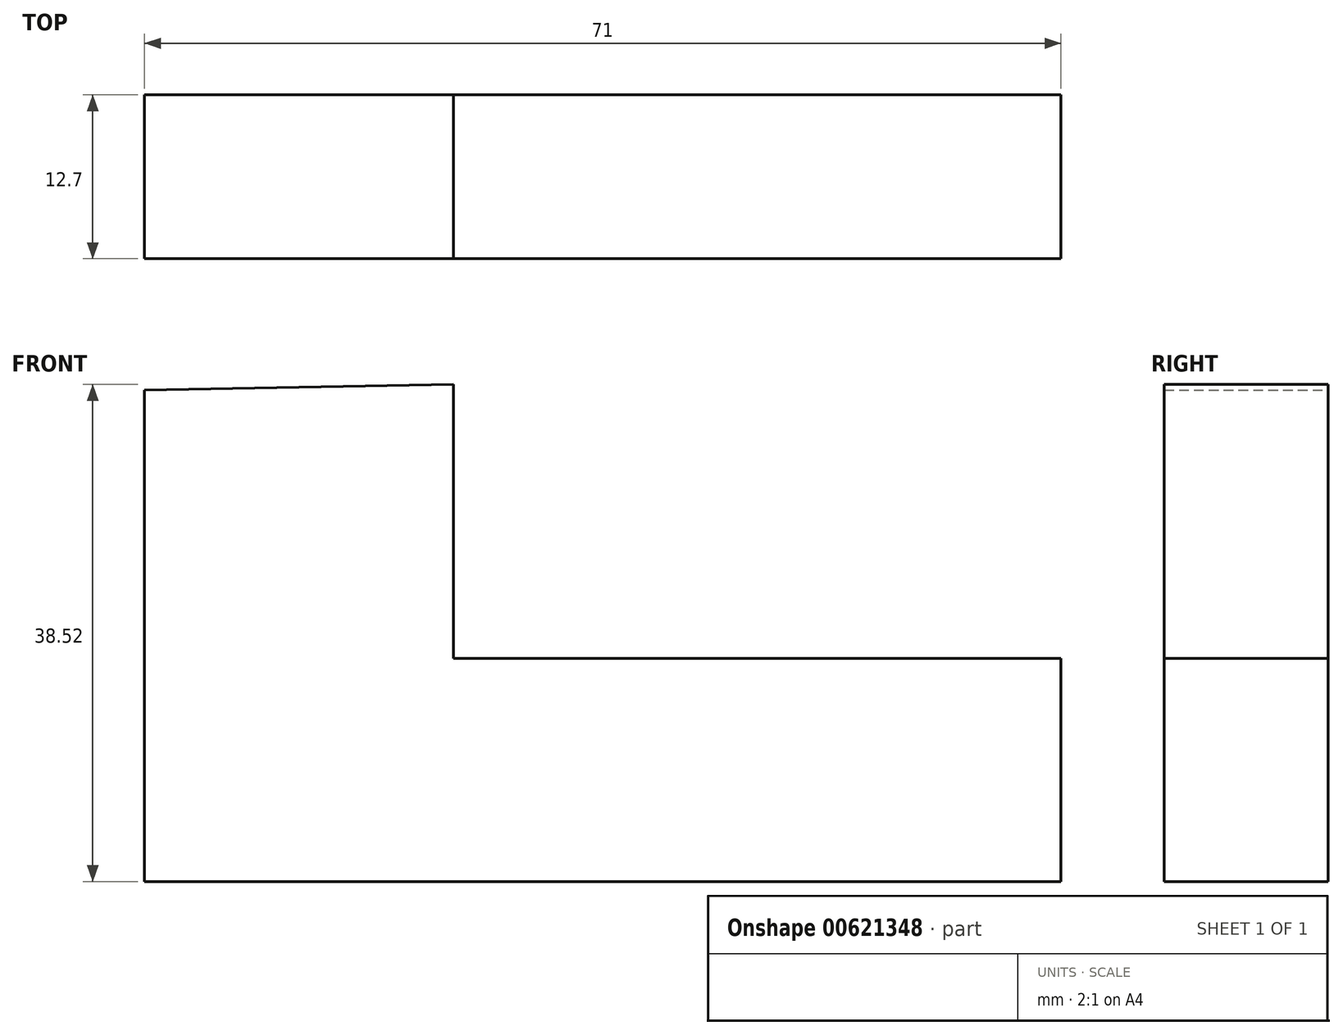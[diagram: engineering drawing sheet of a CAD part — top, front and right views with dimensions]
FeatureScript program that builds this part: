
annotation { "Feature Type Name" : "Feature", "Feature Type Description" : "" }
export const myFeature = defineFeature(function(context is Context, id is Id, definition is map)
    precondition{}
    {
        {
            var Q0;
            Q0=qCreatedBy(makeId("Front.planeOp"),FACE);
            var sketch = newSketch(context, id + "F0", { "sketchPlane" : qUnion([Q0])});
            skLineSegment(sketch, "E0", {"start": v(0, 38.1) * mm, "end": v(0, 0) * mm});
            skLineSegment(sketch, "E1", {"start": v(0, 0) * mm, "end": v(71, 0) * mm});
            skLineSegment(sketch, "E2", {"start": v(71, 0) * mm, "end": v(71, 17.28) * mm});
            skLineSegment(sketch, "E3", {"start": v(71, 17.28) * mm, "end": v(23.94, 17.28) * mm});
            skLineSegment(sketch, "E4", {"start": v(23.94, 17.28) * mm, "end": v(23.94, 38.52) * mm});
            skLineSegment(sketch, "E5", {"start": v(23.94, 38.52) * mm, "end": v(0, 38.1) * mm});
            skSolve(sketch);
        }
        {
            var Q0;
            Q0 = qSketchRegion(id + "F0", true);
            extrude(context, id + "F1", {"entities" : qUnion([Q0]), "depth" : 12.7 * mm, "offsetDistance" : 25.4 * mm});
        }
    });
